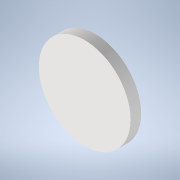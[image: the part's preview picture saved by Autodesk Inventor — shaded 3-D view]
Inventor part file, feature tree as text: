
AUTODESK INVENTOR PART (.ipt)
format: ipt  version: 2022 (Build 260153000, 153)  size: 131,584 bytes
history: native  units: mm
features: extrude x5, sketch x5, reference x2, other x2
ambient origin geometry x8: Origin, YZ Plane, XZ Plane, XY Plane, X Axis, Y Axis, Z Axis, Center Point
bodies: Solid1 (feature_tree)
feature tree (14):
  extrude  "Extrusion1"  Depth=2.4mm TaperAngle=0.0deg
  extrude  "Extrusion2"  Depth=5.4mm
  extrude  "Extrusion3"  Depth=2.4mm
  extrude  "Extrusion4"  Depth=2.8mm
  extrude  "Extrusion5"  Depth=1.0mm
  sketch  "Sketch3"  dims[d0=20.8mm d1=2.4mm d2=0.0mm]
  reference  "Reference1"
  reference  "Reference2"
  sketch  "Sketch4"  dims[d3=8.7mm d4=5.4mm]
  sketch  "Sketch5"  dims[d5=2.4mm d6=0.0mm d7=5.4mm]
  sketch  "Sketch6"  dims[d8=2.8mm d9=0.0mm d10=5.7mm]
  sketch  "Sketch7"  dims[d11=1.0mm d12=0.0mm d13=3.0mm d14=0.0mm d15=0.0mm]
  other  "EnsambleCuerpo.iam"
  other  "Base3:1"
